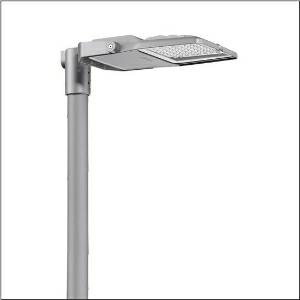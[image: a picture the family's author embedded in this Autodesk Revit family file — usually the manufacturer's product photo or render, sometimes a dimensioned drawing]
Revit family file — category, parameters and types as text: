
# Revit family: floodlight_fl_21_mini___pl52_5xa7776b4d3a_8fbb
name_source: partatom
category: Lighting Fixtures
units: mm (PartAtom-declared; Revit-internal decimal feet)

## family parameters
Cut with Voids When Loaded = No
Host = Face
Light Source = No
Part Type = Normal
Room Calculation Point = No
Round Connector Dimension = Use Diameter
Shared = No

## types (1)
- --- (1 x LED, 6480 lm, 45.7 W, 4000K)
    Apparent Load = 46 VA
    CIE Flux Codes = 26 60 98 100 100
    Color Rendering = 70
    Color Temperature = 4000K
    Default Elevation = 1800 mm
    Description = Floodlight FL 21 mini, floodlight, primary light control with lens, of PMMA, primary optical cover: protective disc, of toughened safety glass, transparent, light distribution: PL52, light emission: direct distribution, installation type: surface-mounted, LED, High Power LED, rated luminous flux: 6.480lm, luminous efficacy: 142lm/W, light colour: 740, colour temperature: 4000K, control gear: D4iSmart Interface (Zhaga), control: overheat protection, constant luminous flux control, time-dependent luminous flux control, flexible luminous flux parameterisation, pre-setting: logarithmic dimming characteristic, with terminal, 6-pole, mains connection: 220..240V, AC, 50/60Hz, start of lifetime: 46W, end of service life: 48W, reduction: 22W, mast bracket, of diecast aluminium, powder-coated, Siteco® metallic grey (DB 702S), corrosivity category C5 mid according to DIN EN ISO 12944, suitable for swimming pools, chlorine-resistant, sealing non-destructively replaceable, mast bracket, of steel, galvanised, powder-coated, Siteco® metallic grey (DB 702S), Smart Interface below and above, protection rating (complete): IP66, insulation class (complete): insulation class II (safety insulation), certification: CE, ENEC, VDE, protection symbol: D, impact resistance: IK08, permissible operating ambient temperature: -40..+40°C, permissible operating ambient temperature for outdoor applications: -40..+50°C, standard: DIN EN 12944, LABS conformity tested according to VDMA 24364:2018-05, packaging unit: 1 piece

Light Distribution: PL52
    Height = 70 mm
    Lamp = 1 x LED
    Lamp Light Flux = 6480 lm
    Lamp Power = 45.7 W
    Lamp count = 1
    Length = 485 mm
    Luminous efficacy = 142 lm/W
    Manufacturer = Siteco
    ModVariant = No
    Model = 5XA7776B4D3A
    Number of Poles = 1
    OnlyDefault = Yes
    Power Factor = 1
    Product Name = Floodlight FL 21 mini | PL52
    Product group = floodlight | pylon annexe
    ProductGroupID = 6201
    Protection Class = Protection class II
    Protection Degree = IP 66
    RLX_Detail_Level = 1
    RLX_Emergency_Light_Flux = 0 lm
    RLX_Emergency_Type = 0
    RLX_Emergency_Type_DB = No
    RlxData = <blob elided: 101117 chars, md5=ff8f0998>
    Socket = socket
    Standby Power = 0 W
    System Light Flux = 6480 lm
    System Power = 46 W
    Type Comments = factory setting: luminous flux: 100 % | dim-lin: 254 | 463 mA
    Type Image = l_1007125.jpg
    URL = http://relux.com
    VarID = @adj_117037
    Voltage = 0 V
    Weight = 0.00 kg
    Width = 337 mm

## geometry (parser evidence)
native form markers: Blend x4, Sweep x12
no freeform markers — native parametric forms only
